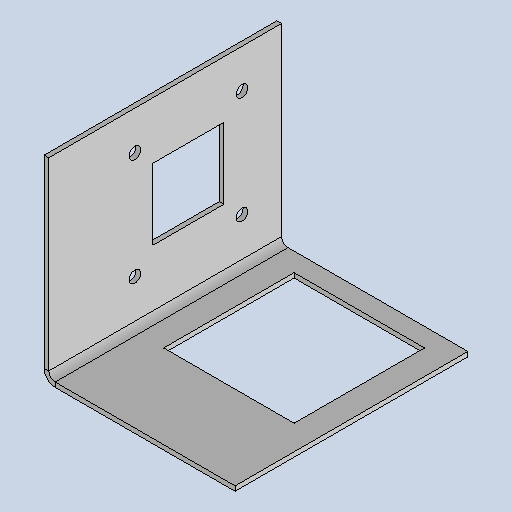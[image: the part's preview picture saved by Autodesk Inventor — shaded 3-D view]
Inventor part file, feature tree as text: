
AUTODESK INVENTOR PART (.ipt)
format: ipt  version: 2025.3 (Build 293356030, 356C)  size: 237,056 bytes
history: native  units: mm
features: other x5, sheet_metal_op x4, sketch x4
ambient origin geometry x8: Origin, YZ Plane, XZ Plane, XY Plane, X Axis, Y Axis, Z Axis, Center Point
bodies: Body1 (feature_tree)
feature tree (13):
  sheet_metal_op  "Face3"
  sheet_metal_op  "Flange3"
  sketch  "Sketch1"  dims[d154=82.0mm]
  other  "Plate5"
  sketch  "Sketch7"  dims[d155=100.0mm]
  other  "Plate6"
  sheet_metal_op  "Bend3"
  sheet_metal_op  "Corner3"
  sketch  "Sketch8"  dims[d156=2.0mm]
  sketch  "Sketch9"  dims[d157=2.0mm d158=1.0mm d159=4.0mm d160=2.75mm d161=84.0mm d162=90.0deg d163=2.75mm d164=8.0mm d165=2.0mm d166=2.75mm d167=56.0mm d168=56.0mm d169=8.0mm d170=2.0mm d171=0.0mm d174=30.5mm d175=30.5mm d176=5.0mm d179=40.0mm d180=51.0mm d181=21.92031mm d182=2.0mm d183=0.0mm d184=46.0mm]
  other  "Cut1"
  other  "Cut2"
  other  "Definition1"
